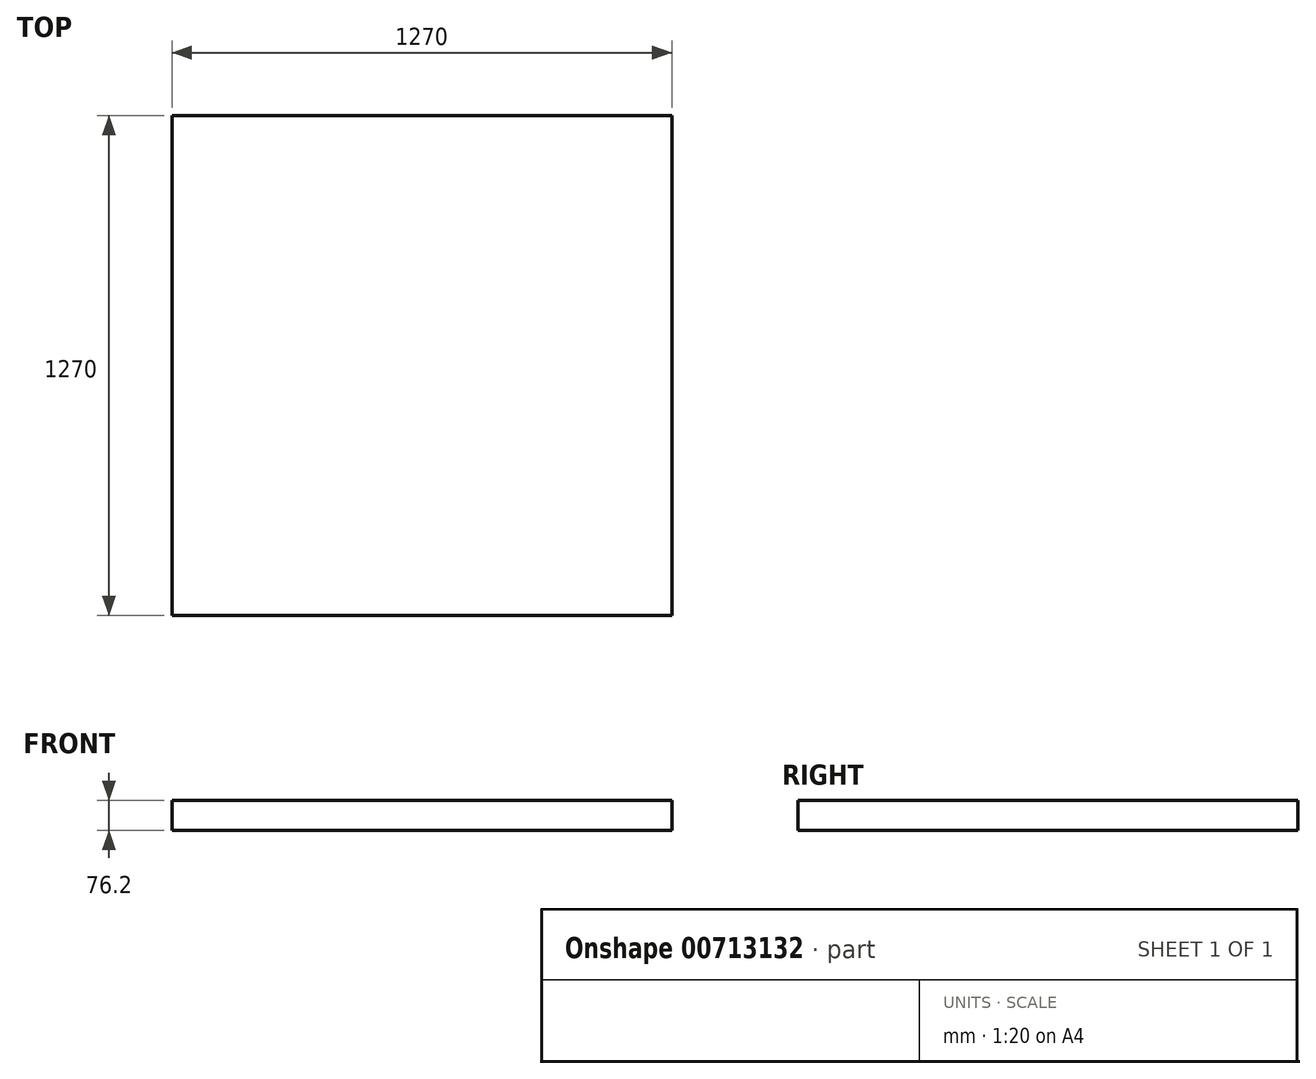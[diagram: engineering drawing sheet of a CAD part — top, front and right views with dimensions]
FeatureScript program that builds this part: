
annotation { "Feature Type Name" : "Feature", "Feature Type Description" : "" }
export const myFeature = defineFeature(function(context is Context, id is Id, definition is map)
    precondition{}
    {
        {
            var Q0;
            Q0=qCreatedBy(makeId("Top.planeOp"),FACE);
            var sketch = newSketch(context, id + "F0", { "sketchPlane" : qUnion([Q0])});
            skLineSegment(sketch, "E0.bottom", {"start": v(-635, 635) * mm, "end": v(635, 635) * mm});
            skLineSegment(sketch, "E0.top", {"start": v(-635, -635) * mm, "end": v(635, -635) * mm});
            skLineSegment(sketch, "E0.left", {"start": v(-635, 635) * mm, "end": v(-635, -635) * mm});
            skLineSegment(sketch, "E0.right", {"start": v(635, 635) * mm, "end": v(635, -635) * mm});
            skPoint(sketch, "E0.middle", {"position": v(0, 0) * mm});
            skSolve(sketch);
        }
        {
            var Q0;
            Q0 = qSketchRegion(id + "F0", true);
            extrude(context, id + "F1", {"entities" : qUnion([Q0]), "depth" : 76.2 * mm, "offsetDistance" : 25.4 * mm});
        }
    });
